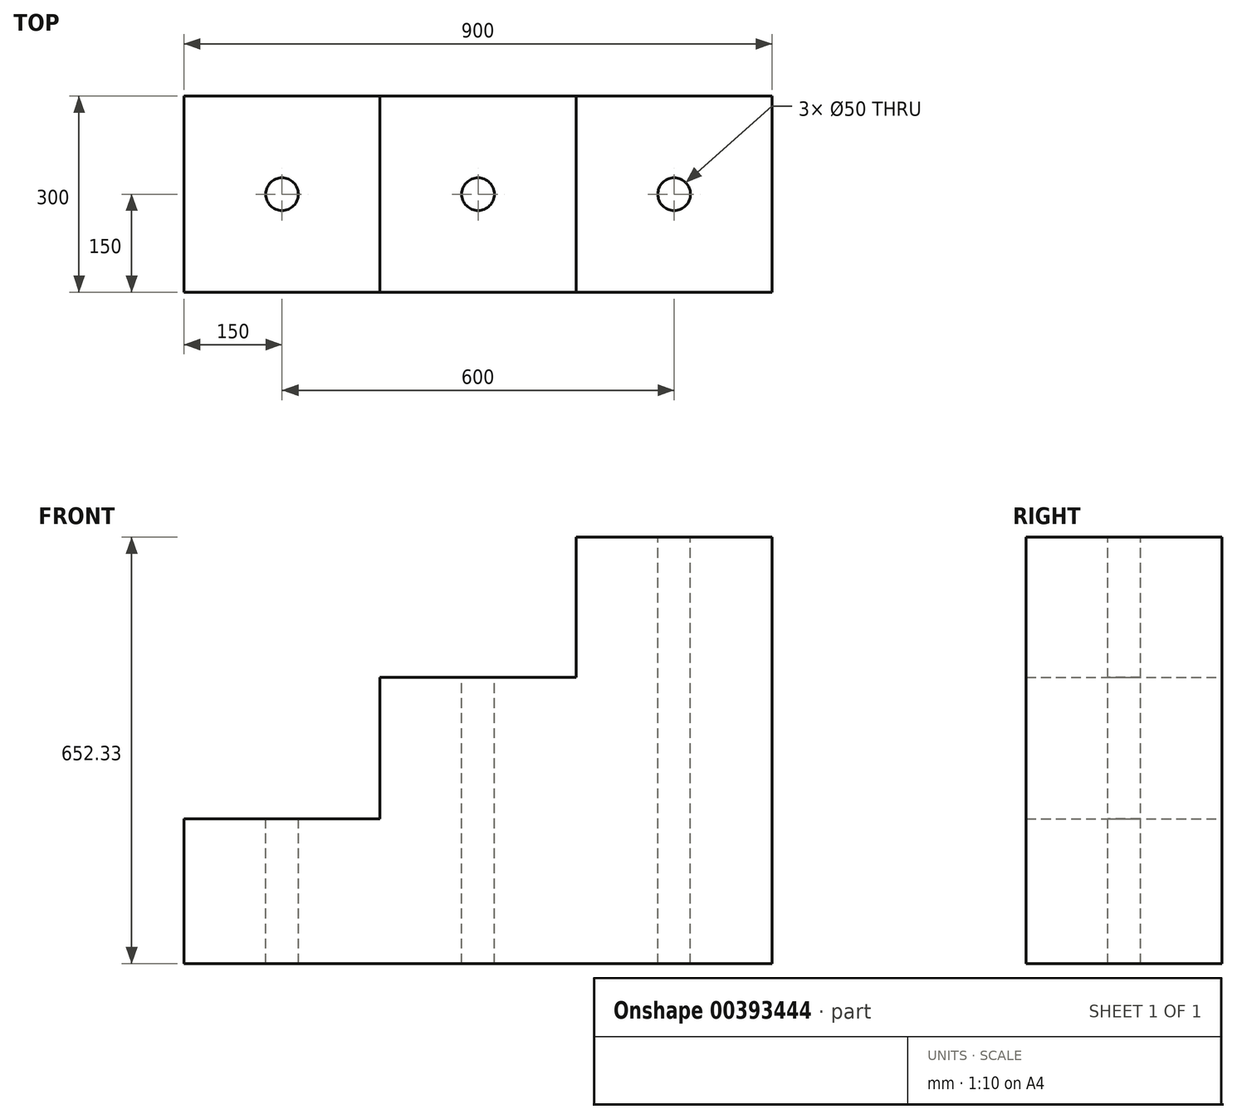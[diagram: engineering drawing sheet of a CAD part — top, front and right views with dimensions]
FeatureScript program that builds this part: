
annotation { "Feature Type Name" : "Feature", "Feature Type Description" : "" }
export const myFeature = defineFeature(function(context is Context, id is Id, definition is map)
    precondition{}
    {
        {
            var Q0;
            Q0=qCreatedBy(makeId("Front.planeOp"),FACE);
            var sketch = newSketch(context, id + "F0", { "sketchPlane" : qUnion([Q0])});
            skLineSegment(sketch, "E0", {"start": v(0, 0) * mm, "end": v(900, 0) * mm});
            skLineSegment(sketch, "E1", {"start": v(900, 0) * mm, "end": v(900, 652.33) * mm});
            skLineSegment(sketch, "E2", {"start": v(900, 652.33) * mm, "end": v(600, 652.33) * mm});
            skLineSegment(sketch, "E3", {"start": v(600, 652.33) * mm, "end": v(600, 437.84) * mm});
            skLineSegment(sketch, "E4", {"start": v(600, 437.84) * mm, "end": v(300, 437.84) * mm});
            skLineSegment(sketch, "E5", {"start": v(300, 437.84) * mm, "end": v(300, 221.13) * mm});
            skLineSegment(sketch, "E6", {"start": v(300, 221.13) * mm, "end": v(0, 221.13) * mm});
            skLineSegment(sketch, "E7", {"start": v(0, 221.13) * mm, "end": v(0, 0) * mm});
            skSolve(sketch);
        }
        {
            var Q0;
            Q0 = qSketchRegion(id + "F0", true);
            extrude(context, id + "F1", {"entities" : qUnion([Q0]), "depth" : 300 * mm});
        }
        {
            var Q0;
            Q0=makeQuery(id+"F1.opExtrude","SWEPT_FACE",FACE,{"disambiguationData":[OSD([sQuery(id+"F0.wireOp",EDGE,"E4")])]});
            var sketch = newSketch(context, id + "F2", { "sketchPlane" : qUnion([Q0])});
            skCircle(sketch, "E8", {"center": v(450, -150) * mm, "radius": 25 * mm});
            skPoint(sketch, "E8.centerSnap0", {"position": v(300, -150) * mm});
            skPoint(sketch, "E8.centerSnap1", {"position": v(450, 0) * mm});
            skSolve(sketch);
        }
        {
            var Q0;
            Q0=sQuery(id+"F2.wireOp",VERTEX,"E8.center");
            var Q1;
            Q1=makeQuery(id+"F1.opExtrude","SWEPT_BODY",BODY,{"disambiguationData":[OSD([sQuery(id+"F0.wireOp",EDGE,"E0"),sQuery(id+"F0.wireOp",EDGE,"E1"),sQuery(id+"F0.wireOp",EDGE,"E2"),sQuery(id+"F0.wireOp",EDGE,"E3"),sQuery(id+"F0.wireOp",EDGE,"E4"),sQuery(id+"F0.wireOp",EDGE,"E5"),sQuery(id+"F0.wireOp",EDGE,"E6"),sQuery(id+"F0.wireOp",EDGE,"E7")])]});
            hole(context, id + "F3", {"style" : HoleStyle.SIMPLE, "endStyle" : HoleEndStyle.THROUGH, "holeDiameter" : 50 * mm, "isTappedThrough" : true, "tappedDepth" : 12 * mm, "tapClearance" : 3, "locations" : qUnion([Q0]), "scope" : qUnion([Q1])});
        }
        {
            var Q0;
            Q0=makeQuery(id+"F1.opExtrude","SWEPT_FACE",FACE,{"disambiguationData":[OSD([sQuery(id+"F0.wireOp",EDGE,"E6")])]});
            var sketch = newSketch(context, id + "F4", { "sketchPlane" : qUnion([Q0])});
            skCircle(sketch, "E9", {"center": v(150, -150) * mm, "radius": 25 * mm});
            skPoint(sketch, "E9.centerSnap0", {"position": v(0, -150) * mm});
            skPoint(sketch, "E9.centerSnap1", {"position": v(150, 0) * mm});
            skSolve(sketch);
        }
        {
            var Q0;
            Q0=sQuery(id+"F4.wireOp",VERTEX,"E9.center");
            var Q1;
            Q1=makeQuery(id+"F1.opExtrude","SWEPT_BODY",BODY,{"disambiguationData":[OSD([sQuery(id+"F0.wireOp",EDGE,"E0"),sQuery(id+"F0.wireOp",EDGE,"E1"),sQuery(id+"F0.wireOp",EDGE,"E2"),sQuery(id+"F0.wireOp",EDGE,"E3"),sQuery(id+"F0.wireOp",EDGE,"E4"),sQuery(id+"F0.wireOp",EDGE,"E5"),sQuery(id+"F0.wireOp",EDGE,"E6"),sQuery(id+"F0.wireOp",EDGE,"E7")])]});
            hole(context, id + "F5", {"style" : HoleStyle.SIMPLE, "endStyle" : HoleEndStyle.THROUGH, "holeDiameter" : 50 * mm, "isTappedThrough" : true, "tappedDepth" : 12 * mm, "tapClearance" : 3, "locations" : qUnion([Q0]), "scope" : qUnion([Q1])});
        }
        {
            var Q0;
            Q0=makeQuery(id+"F1.opExtrude","SWEPT_FACE",FACE,{"disambiguationData":[OSD([sQuery(id+"F0.wireOp",EDGE,"E2")])]});
            var sketch = newSketch(context, id + "F6", { "sketchPlane" : qUnion([Q0])});
            skCircle(sketch, "E10", {"center": v(750, -150) * mm, "radius": 25 * mm});
            skPoint(sketch, "E10.centerSnap0", {"position": v(600, -150) * mm});
            skPoint(sketch, "E10.centerSnap1", {"position": v(750, 0) * mm});
            skSolve(sketch);
        }
        {
            var Q0;
            Q0=sQuery(id+"F6.wireOp",VERTEX,"E10.center");
            var Q1;
            Q1=makeQuery(id+"F1.opExtrude","SWEPT_BODY",BODY,{"disambiguationData":[OSD([sQuery(id+"F0.wireOp",EDGE,"E0"),sQuery(id+"F0.wireOp",EDGE,"E1"),sQuery(id+"F0.wireOp",EDGE,"E2"),sQuery(id+"F0.wireOp",EDGE,"E3"),sQuery(id+"F0.wireOp",EDGE,"E4"),sQuery(id+"F0.wireOp",EDGE,"E5"),sQuery(id+"F0.wireOp",EDGE,"E6"),sQuery(id+"F0.wireOp",EDGE,"E7")])]});
            hole(context, id + "F7", {"style" : HoleStyle.SIMPLE, "endStyle" : HoleEndStyle.THROUGH, "holeDiameter" : 50 * mm, "isTappedThrough" : true, "tappedDepth" : 12 * mm, "tapClearance" : 3, "locations" : qUnion([Q0]), "scope" : qUnion([Q1])});
        }
    });
